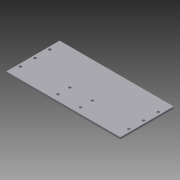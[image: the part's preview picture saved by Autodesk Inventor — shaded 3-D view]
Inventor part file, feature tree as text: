
AUTODESK INVENTOR PART (.ipt)
format: ipt  version: 2012 (Build 160160000, 160)  size: 104,448 bytes
history: native  units: mm
features: reference x10, sketch x2, extrude x1, hole x1
ambient origin geometry x8: Origin, YZ Plane, XZ Plane, XY Plane, X Axis, Y Axis, Z Axis, Center Point
feature tree (14):
  extrude  "Extrusion2"  Depth=91.44mm
  hole  "Hole2"  [1 undecoded]
  sketch  "Sketch1"  dims[d25=3.175mm d26=0.0mm d27=91.44mm]
  sketch  "Sketch3"  dims[d28=195.58mm d29=4.4958mm d30=19.05mm d31=8.4328mm d32=6.35mm d33=14.3117mm d34=25.4mm d35=20.594885mm]
  reference  "Reference1"
  reference  "Reference2"
  reference  "Reference3"
  reference  "Reference4"
  reference  "Reference5"
  reference  "Reference6"
  reference  "Reference7"
  reference  "Reference8"
  reference  "Reference9"
  reference  "Reference10"
note: 1 required parameter value undecoded (feature->parameter linkage not recoverable at this tier; creation-order binding heuristic only, values carry confidence <= 0.55)
